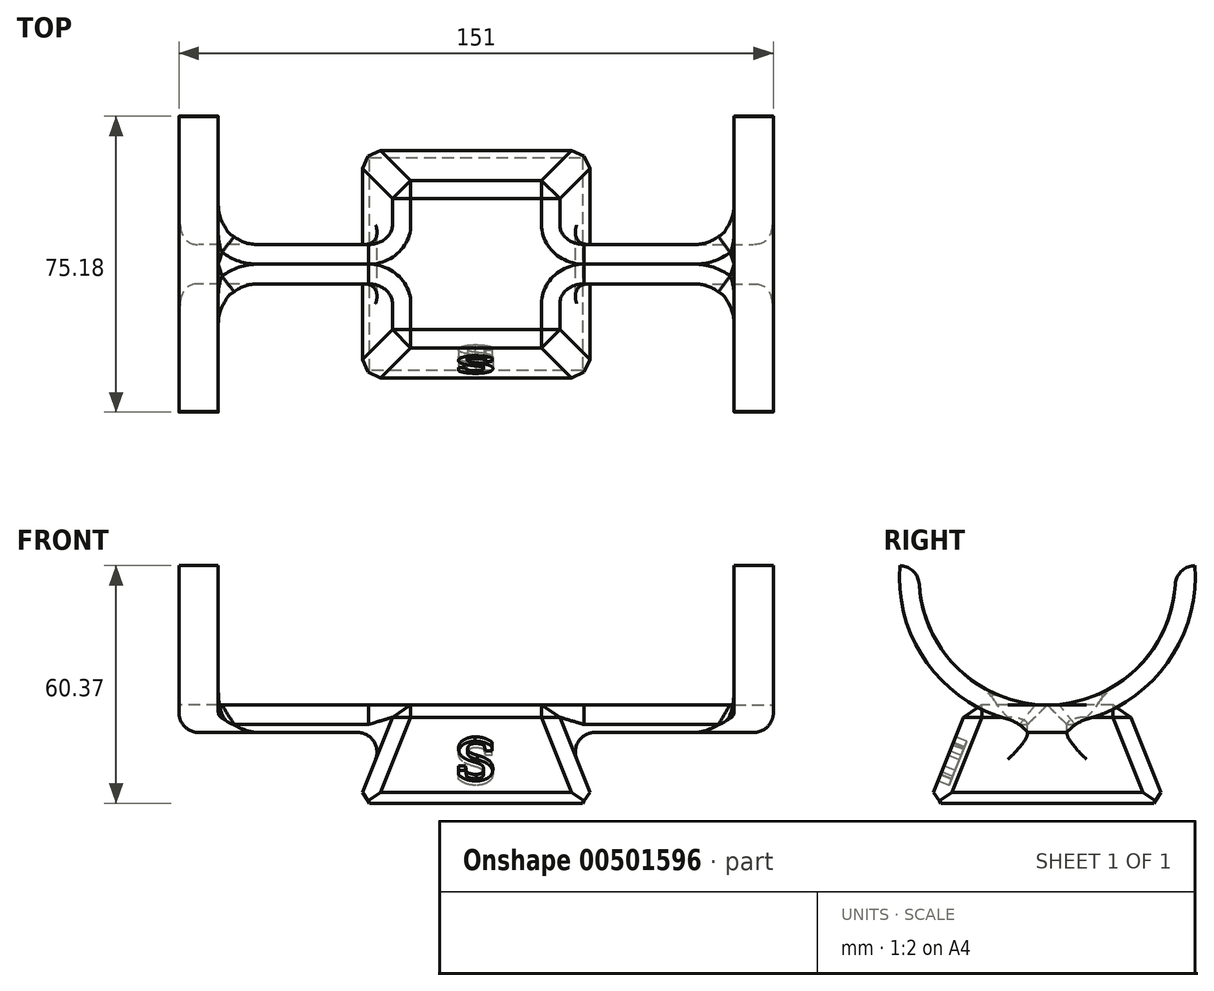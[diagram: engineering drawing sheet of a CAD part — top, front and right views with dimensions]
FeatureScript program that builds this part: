
annotation { "Feature Type Name" : "Feature", "Feature Type Description" : "" }
export const myFeature = defineFeature(function(context is Context, id is Id, definition is map)
    precondition{}
    {
        {
            var Q0;
            Q0=qCreatedBy(makeId("Top.planeOp"),FACE);
            var sketch = newSketch(context, id + "F0", { "sketchPlane" : qUnion([Q0])});
            skLineSegment(sketch, "E0.bottom", {"start": v(-30, 30) * mm, "end": v(30, 30) * mm});
            skLineSegment(sketch, "E0.top", {"start": v(-30, -30) * mm, "end": v(30, -30) * mm});
            skLineSegment(sketch, "E0.left", {"start": v(-30, 30) * mm, "end": v(-30, -30) * mm});
            skLineSegment(sketch, "E0.right", {"start": v(30, 30) * mm, "end": v(30, -30) * mm});
            skPoint(sketch, "E0.middle", {"position": v(0, 0) * mm});
            skSolve(sketch);
        }
        {
            var Q0;
            Q0=qCreatedBy(makeId("Top.planeOp"),FACE);
            cPlane(context, id + "F1", {"entities" : qUnion([Q0]), "cplaneType" : CPlaneType.OFFSET, "offset" : 25 * mm, "width" : 150 * mm, "height" : 150 * mm});
        }
        {
            var Q0;
            Q0=qCreatedBy(id+"F1.planeOp",FACE);
            var sketch = newSketch(context, id + "F2", { "sketchPlane" : qUnion([Q0])});
            skLineSegment(sketch, "E1.bottom", {"start": v(-20, 20) * mm, "end": v(20, 20) * mm});
            skLineSegment(sketch, "E1.top", {"start": v(-20, -20) * mm, "end": v(20, -20) * mm});
            skLineSegment(sketch, "E1.left", {"start": v(-20, 20) * mm, "end": v(-20, -20) * mm});
            skLineSegment(sketch, "E1.right", {"start": v(20, 20) * mm, "end": v(20, -20) * mm});
            skPoint(sketch, "E1.middle", {"position": v(0, 0) * mm});
            skSolve(sketch);
        }
        {
            var Q0;
            Q0=makeQuery(id+"F0.imprint","IMPRINT",FACE,{"disambiguationData":[TD([[makeQuery(id+"F0.imprint","IMPRINT",EDGE,{"derivedFrom":sQuery(id+"F0.wireOp",EDGE,"E0.bottom")}),-1.0]])]});
            var Q1;
            Q1=makeQuery(id+"F2.imprint","IMPRINT",FACE,{"disambiguationData":[TD([[makeQuery(id+"F2.imprint","IMPRINT",EDGE,{"derivedFrom":sQuery(id+"F2.wireOp",EDGE,"E1.bottom")}),-1.0]])]});
            loft(context, id + "F3", {"sheetProfilesArray" : [{ "sheetProfileEntities" : qUnion([Q0]) }, { "sheetProfileEntities" : qUnion([Q1]) }]});
        }
        {
            var Q0;
            Q0=qCreatedBy(id+"F1.planeOp",FACE);
            var sketch = newSketch(context, id + "F4", { "sketchPlane" : qUnion([Q0])});
            skLineSegment(sketch, "E2.bottom", {"start": v(-75.5, 5) * mm, "end": v(75.5, 5) * mm});
            skLineSegment(sketch, "E2.top", {"start": v(-75.5, -5) * mm, "end": v(75.5, -5) * mm});
            skLineSegment(sketch, "E2.left", {"start": v(-75.5, 5) * mm, "end": v(-75.5, -5) * mm});
            skLineSegment(sketch, "E2.right", {"start": v(75.5, 5) * mm, "end": v(75.5, -5) * mm});
            skPoint(sketch, "E2.middle", {"position": v(0, 0) * mm});
            skSolve(sketch);
        }
        {
            var Q0;
            Q0=makeQuery(id+"F4.imprint","IMPRINT",FACE,{"disambiguationData":[TD([[makeQuery(id+"F4.imprint","IMPRINT",EDGE,{"derivedFrom":sQuery(id+"F4.wireOp",EDGE,"E2.bottom")}),-1.0]])]});
            extrude(context, id + "F5", {"entities" : qUnion([Q0]), "operationType" : NewBodyOperationType.ADD, "oppositeDirection" : true, "depth" : 7 * mm});
        }
        {
            var Q0;
            Q0=makeQuery(id+"F5.opExtrude","SWEPT_FACE",FACE,{"disambiguationData":[OSD([sQuery(id+"F4.wireOp",EDGE,"E2.right")])]});
            var sketch = newSketch(context, id + "F6", { "sketchPlane" : qUnion([Q0])});
            skArc(sketch, "E3", {"start": v(-32.5, 60) * mm, "mid": v(-23.88, 35.41) * mm, "end": v(0, 25) * mm});
            skArc(sketch, "E4.MirrorCS", {"start": v(32.5, 60) * mm, "mid": v(23.88, 35.41) * mm, "end": v(0, 25) * mm});
            skArc(sketch, "E5.0", {"start": v(37.49, 60.37) * mm, "mid": v(27.55, 32.01) * mm, "end": v(0, 20) * mm});
            skArc(sketch, "E5.1", {"start": v(-37.49, 60.37) * mm, "mid": v(-27.55, 32.01) * mm, "end": v(0, 20) * mm});
            skLineSegment(sketch, "E6", {"start": v(-32.5, 60) * mm, "end": v(-37.49, 60.37) * mm});
            skLineSegment(sketch, "E7", {"start": v(32.5, 60) * mm, "end": v(37.49, 60.37) * mm});
            skSolve(sketch);
        }
        {
            var Q0;
            Q0 = qSketchRegion(id + "F6", true);
            extrude(context, id + "F7", {"entities" : qUnion([Q0]), "operationType" : NewBodyOperationType.ADD, "oppositeDirection" : true, "depth" : 10 * mm});
        }
        {
            var Q0;
            {var subQ0=sQuery(id+"F4.wireOp",EDGE,"E2.right");var subQ2=sQuery(id+"F4.wireOp",EDGE,"E2.top");Q0=makeQuery(id+"F7.boolean.opBoolean","INTERSECT",EDGE,{"derivedFrom":[makeQuery(id+"F5.boolean.opBoolean","SPLIT",FACE,{"disambiguationData":[TD([makeQuery(id+"F5.opExtrude","SWEPT_FACE",FACE,{"disambiguationData":[OSD([subQ0])]})])],"derivedFrom":makeQuery(id+"F5.opExtrude","SWEPT_FACE",FACE,{"disambiguationData":[OSD([subQ2])]})}),makeQuery(id+"F7.opExtrude","SWEPT_FACE",FACE,{"disambiguationData":[OSD([sQuery(id+"F6.wireOp",EDGE,"E5.0"),sQuery(id+"F6.wireOp",EDGE,"E5.1")])]})]});}
            var Q1;
            {var subQ0=sQuery(id+"F4.wireOp",EDGE,"E2.right");var subQ3=sQuery(id+"F4.wireOp",EDGE,"E2.bottom");Q1=makeQuery(id+"F7.boolean.opBoolean","INTERSECT",EDGE,{"derivedFrom":[makeQuery(id+"F5.boolean.opBoolean","SPLIT",FACE,{"disambiguationData":[TD([makeQuery(id+"F5.opExtrude","SWEPT_FACE",FACE,{"disambiguationData":[OSD([subQ0])]})])],"derivedFrom":makeQuery(id+"F5.opExtrude","SWEPT_FACE",FACE,{"disambiguationData":[OSD([subQ3])]})}),makeQuery(id+"F7.opExtrude","SWEPT_FACE",FACE,{"disambiguationData":[OSD([sQuery(id+"F6.wireOp",EDGE,"E5.0"),sQuery(id+"F6.wireOp",EDGE,"E5.1")])]})]});}
            var Q2;
            {var subQ0=sQuery(id+"F4.wireOp",EDGE,"E2.right");var subQ3=sQuery(id+"F4.wireOp",EDGE,"E2.bottom");Q2=makeQuery(id+"F7.boolean.opBoolean","INTERSECT",EDGE,{"derivedFrom":[makeQuery(id+"F5.boolean.opBoolean","SPLIT",FACE,{"disambiguationData":[TD([makeQuery(id+"F5.opExtrude","SWEPT_FACE",FACE,{"disambiguationData":[OSD([subQ0])]})])],"derivedFrom":makeQuery(id+"F5.opExtrude","SWEPT_FACE",FACE,{"disambiguationData":[OSD([subQ3])]})}),makeQuery(id+"F7.opExtrude","CAP_FACE",FACE,{"disambiguationData":[OSD([sQuery(id+"F6.wireOp",EDGE,"E3"),sQuery(id+"F6.wireOp",EDGE,"E4.MirrorCS"),sQuery(id+"F6.wireOp",EDGE,"E5.0"),sQuery(id+"F6.wireOp",EDGE,"E5.1"),sQuery(id+"F6.wireOp",EDGE,"E6"),sQuery(id+"F6.wireOp",EDGE,"E7")])],"isStart":false})]});}
            var Q3;
            {var subQ0=sQuery(id+"F4.wireOp",EDGE,"E2.right");var subQ2=sQuery(id+"F4.wireOp",EDGE,"E2.top");Q3=makeQuery(id+"F7.boolean.opBoolean","INTERSECT",EDGE,{"derivedFrom":[makeQuery(id+"F5.boolean.opBoolean","SPLIT",FACE,{"disambiguationData":[TD([makeQuery(id+"F5.opExtrude","SWEPT_FACE",FACE,{"disambiguationData":[OSD([subQ0])]})])],"derivedFrom":makeQuery(id+"F5.opExtrude","SWEPT_FACE",FACE,{"disambiguationData":[OSD([subQ2])]})}),makeQuery(id+"F7.opExtrude","CAP_FACE",FACE,{"disambiguationData":[OSD([sQuery(id+"F6.wireOp",EDGE,"E3"),sQuery(id+"F6.wireOp",EDGE,"E4.MirrorCS"),sQuery(id+"F6.wireOp",EDGE,"E5.0"),sQuery(id+"F6.wireOp",EDGE,"E5.1"),sQuery(id+"F6.wireOp",EDGE,"E6"),sQuery(id+"F6.wireOp",EDGE,"E7")])],"isStart":false})]});}
            fillet(context, id + "F8", {"entities" : qUnion([Q0, Q1, Q2, Q3]), "radius" : 10 * mm, "tangentPropagation" : true, "allowEdgeOverflow" : false});
        }
        {
            var Q0;
            Q0=makeQuery(id+"F7.boolean.opBoolean","INTERSECT",EDGE,{"disambiguationData":[OD(1.0)],"derivedFrom":[makeQuery(id+"F5.boolean.opBoolean","MERGE",FACE,{"derivedFrom":[makeQuery(id+"F3.opLoft","CAP_FACE",FACE,{"disambiguationData":[OSD([makeQuery(id+"F2.imprint","IMPRINT",FACE,{"disambiguationData":[TD([[makeQuery(id+"F2.imprint","IMPRINT",EDGE,{"derivedFrom":sQuery(id+"F2.wireOp",EDGE,"E1.bottom")}),-1.0]])]})])],"isStart":true}),makeQuery(id+"F5.opExtrude","CAP_FACE",FACE,{"disambiguationData":[OSD([sQuery(id+"F4.wireOp",EDGE,"E2.bottom"),sQuery(id+"F4.wireOp",EDGE,"E2.top"),sQuery(id+"F4.wireOp",EDGE,"E2.left"),sQuery(id+"F4.wireOp",EDGE,"E2.right")])],"isStart":true})]}),makeQuery(id+"F7.opExtrude","CAP_FACE",FACE,{"disambiguationData":[OSD([sQuery(id+"F6.wireOp",EDGE,"E3"),sQuery(id+"F6.wireOp",EDGE,"E4.MirrorCS"),sQuery(id+"F6.wireOp",EDGE,"E5.0"),sQuery(id+"F6.wireOp",EDGE,"E5.1"),sQuery(id+"F6.wireOp",EDGE,"E6"),sQuery(id+"F6.wireOp",EDGE,"E7")])],"isStart":false})]});
            fillet(context, id + "F9", {"entities" : qUnion([Q0]), "radius" : 3 * mm, "tangentPropagation" : true, "allowEdgeOverflow" : false});
        }
        {
            var Q0;
            Q0=makeQuery(id+"F5.opExtrude","CAP_EDGE",EDGE,{"disambiguationData":[OSD([sQuery(id+"F4.wireOp",EDGE,"E2.right")])],"isStart":false});
            var Q1;
            Q1=makeQuery(id+"F5.boolean.opBoolean","INTERSECT",EDGE,{"derivedFrom":[makeQuery(id+"F3.opLoft","SWEPT_FACE",FACE,{"disambiguationData":[OSD([sQuery(id+"F0.wireOp",EDGE,"E0.bottom"),sQuery(id+"F0.wireOp",EDGE,"E0.top"),sQuery(id+"F0.wireOp",EDGE,"E0.right"),sQuery(id+"F2.wireOp",EDGE,"E1.bottom"),sQuery(id+"F2.wireOp",EDGE,"E1.top"),sQuery(id+"F2.wireOp",EDGE,"E1.right")])]}),makeQuery(id+"F5.opExtrude","SWEPT_FACE",FACE,{"disambiguationData":[OSD([sQuery(id+"F4.wireOp",EDGE,"E2.bottom")])]})]});
            var Q2;
            Q2=makeQuery(id+"F5.boolean.opBoolean","INTERSECT",EDGE,{"derivedFrom":[makeQuery(id+"F3.opLoft","SWEPT_FACE",FACE,{"disambiguationData":[OSD([sQuery(id+"F0.wireOp",EDGE,"E0.bottom"),sQuery(id+"F0.wireOp",EDGE,"E0.top"),sQuery(id+"F0.wireOp",EDGE,"E0.right"),sQuery(id+"F2.wireOp",EDGE,"E1.bottom"),sQuery(id+"F2.wireOp",EDGE,"E1.top"),sQuery(id+"F2.wireOp",EDGE,"E1.right")])]}),makeQuery(id+"F5.opExtrude","CAP_FACE",FACE,{"disambiguationData":[OSD([sQuery(id+"F4.wireOp",EDGE,"E2.bottom"),sQuery(id+"F4.wireOp",EDGE,"E2.top"),sQuery(id+"F4.wireOp",EDGE,"E2.left"),sQuery(id+"F4.wireOp",EDGE,"E2.right")])],"isStart":false})]});
            var Q3;
            Q3=makeQuery(id+"F5.boolean.opBoolean","INTERSECT",EDGE,{"derivedFrom":[makeQuery(id+"F3.opLoft","SWEPT_FACE",FACE,{"disambiguationData":[OSD([sQuery(id+"F0.wireOp",EDGE,"E0.bottom"),sQuery(id+"F0.wireOp",EDGE,"E0.top"),sQuery(id+"F0.wireOp",EDGE,"E0.right"),sQuery(id+"F2.wireOp",EDGE,"E1.bottom"),sQuery(id+"F2.wireOp",EDGE,"E1.top"),sQuery(id+"F2.wireOp",EDGE,"E1.right")])]}),makeQuery(id+"F5.opExtrude","SWEPT_FACE",FACE,{"disambiguationData":[OSD([sQuery(id+"F4.wireOp",EDGE,"E2.top")])]})]});
            var Q4;
            Q4=makeQuery(id+"F7.opExtrude","SWEPT_EDGE",EDGE,{"disambiguationData":[OSD([sQuery(id+"F6.wireOp",EDGE,"E4.MirrorCS"),sQuery(id+"F6.wireOp",EDGE,"E7")])]});
            var Q5;
            Q5=makeQuery(id+"F7.opExtrude","SWEPT_EDGE",EDGE,{"disambiguationData":[OSD([sQuery(id+"F6.wireOp",EDGE,"E3"),sQuery(id+"F6.wireOp",EDGE,"E6")])]});
            fillet(context, id + "F10", {"entities" : qUnion([Q0, Q1, Q2, Q3, Q4, Q5]), "radius" : 5 * mm, "tangentPropagation" : true, "allowEdgeOverflow" : false});
        }
        {
            var Q0;
            Q0=makeQuery(id+"F3.opLoft","SWEPT_BODY",BODY,{"disambiguationData":[OSD([makeQuery(id+"F0.imprint","IMPRINT",FACE,{"disambiguationData":[TD([[makeQuery(id+"F0.imprint","IMPRINT",EDGE,{"derivedFrom":sQuery(id+"F0.wireOp",EDGE,"E0.bottom")}),-1.0]])]}),makeQuery(id+"F2.imprint","IMPRINT",FACE,{"disambiguationData":[TD([[makeQuery(id+"F2.imprint","IMPRINT",EDGE,{"derivedFrom":sQuery(id+"F2.wireOp",EDGE,"E1.bottom")}),-1.0]])]})])]});
            var Q1;
            Q1=qCreatedBy(makeId("Right.planeOp"),FACE);
            mirror(context, id + "F11", {"operationType" : NewBodyOperationType.ADD, "entities" : qUnion([Q0]), "mirrorPlane" : qUnion([Q1])});
        }
        {
            var Q0;
            Q0=makeQuery(id+"F3.opLoft","MID_CAP_EDGE",EDGE,{"disambiguationData":[OSD([sQuery(id+"F2.wireOp",EDGE,"E1.top"),sQuery(id+"F2.wireOp",EDGE,"E1.left"),sQuery(id+"F2.wireOp",EDGE,"E1.right")])],"capPos":1.0});
            var Q1;
            Q1=makeQuery(id+"F3.opLoft","MID_CAP_EDGE",EDGE,{"disambiguationData":[OSD([sQuery(id+"F2.wireOp",EDGE,"E1.bottom"),sQuery(id+"F2.wireOp",EDGE,"E1.left"),sQuery(id+"F2.wireOp",EDGE,"E1.right")])],"capPos":1.0});
            var Q2;
            Q2=makeQuery(id+"F3.opLoft","SWEPT_EDGE",EDGE,{"disambiguationData":[OSD([sQuery(id+"F0.wireOp",EDGE,"E0.bottom"),sQuery(id+"F0.wireOp",EDGE,"E0.right"),sQuery(id+"F2.wireOp",EDGE,"E1.bottom"),sQuery(id+"F2.wireOp",EDGE,"E1.right")])]});
            var Q3;
            Q3=makeQuery(id+"F3.opLoft","SWEPT_EDGE",EDGE,{"disambiguationData":[OSD([sQuery(id+"F0.wireOp",EDGE,"E0.bottom"),sQuery(id+"F0.wireOp",EDGE,"E0.left"),sQuery(id+"F2.wireOp",EDGE,"E1.bottom"),sQuery(id+"F2.wireOp",EDGE,"E1.left")])]});
            var Q4;
            Q4=makeQuery(id+"F3.opLoft","SWEPT_EDGE",EDGE,{"disambiguationData":[OSD([sQuery(id+"F0.wireOp",EDGE,"E0.top"),sQuery(id+"F0.wireOp",EDGE,"E0.left"),sQuery(id+"F2.wireOp",EDGE,"E1.top"),sQuery(id+"F2.wireOp",EDGE,"E1.left")])]});
            var Q5;
            Q5=makeQuery(id+"F3.opLoft","SWEPT_EDGE",EDGE,{"disambiguationData":[OSD([sQuery(id+"F0.wireOp",EDGE,"E0.top"),sQuery(id+"F0.wireOp",EDGE,"E0.right"),sQuery(id+"F2.wireOp",EDGE,"E1.top"),sQuery(id+"F2.wireOp",EDGE,"E1.right")])]});
            var Q6;
            {var subQ0=sQuery(id+"F4.wireOp",EDGE,"E2.left");var subQ1=sQuery(id+"F4.wireOp",EDGE,"E2.bottom");Q6=makeQuery(id+"F5.boolean.opBoolean","SPLIT",EDGE,{"disambiguationData":[TD([makeQuery(id+"F5.opExtrude","SWEPT_FACE",FACE,{"disambiguationData":[OSD([subQ0])]})])],"derivedFrom":makeQuery(id+"F5.opExtrude","CAP_EDGE",EDGE,{"disambiguationData":[OSD([subQ1])],"isStart":true})});}
            var Q7;
            {var subQ0=sQuery(id+"F4.wireOp",EDGE,"E2.left");var subQ1=sQuery(id+"F4.wireOp",EDGE,"E2.top");Q7=makeQuery(id+"F5.boolean.opBoolean","SPLIT",EDGE,{"disambiguationData":[TD([makeQuery(id+"F5.opExtrude","SWEPT_FACE",FACE,{"disambiguationData":[OSD([subQ0])]})])],"derivedFrom":makeQuery(id+"F5.opExtrude","CAP_EDGE",EDGE,{"disambiguationData":[OSD([subQ1])],"isStart":true})});}
            var Q8;
            {var subQ0=sQuery(id+"F4.wireOp",EDGE,"E2.right");var subQ1=sQuery(id+"F4.wireOp",EDGE,"E2.bottom");Q8=makeQuery(id+"F5.boolean.opBoolean","SPLIT",EDGE,{"disambiguationData":[TD([makeQuery(id+"F5.opExtrude","SWEPT_FACE",FACE,{"disambiguationData":[OSD([subQ0])]})])],"derivedFrom":makeQuery(id+"F5.opExtrude","CAP_EDGE",EDGE,{"disambiguationData":[OSD([subQ1])],"isStart":true})});}
            var Q9;
            {var subQ0=sQuery(id+"F4.wireOp",EDGE,"E2.top");var subQ1=sQuery(id+"F4.wireOp",EDGE,"E2.right");Q9=makeQuery(id+"F5.boolean.opBoolean","SPLIT",EDGE,{"disambiguationData":[TD([makeQuery(id+"F5.opExtrude","SWEPT_FACE",FACE,{"disambiguationData":[OSD([subQ1])]})])],"derivedFrom":makeQuery(id+"F5.opExtrude","CAP_EDGE",EDGE,{"disambiguationData":[OSD([subQ0])],"isStart":true})});}
            chamfer(context, id + "F12", {"entities" : qUnion([Q0, Q1, Q2, Q3, Q4, Q5, Q6, Q7, Q8, Q9]), "width" : 5 * mm, "tangentPropagation" : true});
        }
        {
            var Q0;
            Q0=makeQuery(id+"F11.opPattern","COPY",EDGE,{"derivedFrom":makeQuery(id+"F5.opExtrude","CAP_EDGE",EDGE,{"disambiguationData":[OSD([sQuery(id+"F4.wireOp",EDGE,"E2.left")])],"isStart":false}),"instanceName":"1"});
            var Q1;
            Q1=makeQuery(id+"F5.opExtrude","CAP_EDGE",EDGE,{"disambiguationData":[OSD([sQuery(id+"F4.wireOp",EDGE,"E2.left")])],"isStart":false});
            fillet(context, id + "F13", {"entities" : qUnion([Q0, Q1]), "radius" : 5 * mm, "tangentPropagation" : true, "allowEdgeOverflow" : false});
        }
        {
            var Q0;
            Q0=makeQuery(id+"F3.opLoft","MID_CAP_EDGE",EDGE,{"disambiguationData":[OSD([sQuery(id+"F0.wireOp",EDGE,"E0.bottom"),sQuery(id+"F0.wireOp",EDGE,"E0.left"),sQuery(id+"F0.wireOp",EDGE,"E0.right")])],"capPos":0.0});
            var Q1;
            Q1=makeQuery(id+"F3.opLoft","MID_CAP_EDGE",EDGE,{"disambiguationData":[OSD([sQuery(id+"F0.wireOp",EDGE,"E0.bottom"),sQuery(id+"F0.wireOp",EDGE,"E0.top"),sQuery(id+"F0.wireOp",EDGE,"E0.right")])],"capPos":0.0});
            var Q2;
            Q2=makeQuery(id+"F3.opLoft","MID_CAP_EDGE",EDGE,{"disambiguationData":[OSD([sQuery(id+"F0.wireOp",EDGE,"E0.top"),sQuery(id+"F0.wireOp",EDGE,"E0.left"),sQuery(id+"F0.wireOp",EDGE,"E0.right")])],"capPos":0.0});
            var Q3;
            Q3=makeQuery(id+"F3.opLoft","MID_CAP_EDGE",EDGE,{"disambiguationData":[OSD([sQuery(id+"F0.wireOp",EDGE,"E0.bottom"),sQuery(id+"F0.wireOp",EDGE,"E0.top"),sQuery(id+"F0.wireOp",EDGE,"E0.left")])],"capPos":0.0});
            chamfer(context, id + "F14", {"entities" : qUnion([Q0, Q1, Q2, Q3]), "width" : 2 * mm, "tangentPropagation" : true});
        }
        {
            var Q0;
            Q0=makeQuery(id+"F3.opLoft","SWEPT_FACE",FACE,{"disambiguationData":[OSD([sQuery(id+"F0.wireOp",EDGE,"E0.top"),sQuery(id+"F0.wireOp",EDGE,"E0.left"),sQuery(id+"F0.wireOp",EDGE,"E0.right"),sQuery(id+"F2.wireOp",EDGE,"E1.top"),sQuery(id+"F2.wireOp",EDGE,"E1.left"),sQuery(id+"F2.wireOp",EDGE,"E1.right")])]});
            var sketch = newSketch(context, id + "F15", { "sketchPlane" : qUnion([Q0])});
            skLineSegment(sketch, "E8", {"start": v(0, -11.28) * mm, "end": v(0, 10.78) * mm});
            skText(sketch, "E9", { "text": "S", "fontName": "RobotoSlab-Bold.ttf"});
            const initialGuessF15  = {"E9": [-0.00527, -0.00485, 1, 0, 0.01187]};
            skSetInitialGuess(sketch, initialGuessF15);
            skSolve(sketch);
        }
        {
            var Q0;
            {var subQ6=sQuery(id+"F15.wireOp",EDGE,"E9.sketch_text.stroke-4");Q0=makeQuery(id+"F15.imprint","IMPRINT",FACE,{"disambiguationData":[TD([[makeQuery(id+"F15.imprint","IMPRINT",EDGE,{"derivedFrom":subQ6}),-1.0]])]});}
            var Q1;
            Q1=makeQuery(id+"F15.imprint","IMPRINT",FACE,{"disambiguationData":[TD([[makeQuery(id+"F15.imprint","IMPRINT",EDGE,{"derivedFrom":sQuery(id+"F15.wireOp",EDGE,"E9.sketch_text.stroke-0")}),-1.0]])]});
            var Q2;
            {var subQ8=sQuery(id+"F15.wireOp",EDGE,"E9.sketch_text.stroke-8");Q2=makeQuery(id+"F15.imprint","IMPRINT",FACE,{"disambiguationData":[TD([[makeQuery(id+"F15.imprint","IMPRINT",EDGE,{"derivedFrom":subQ8}),-1.0]])]});}
            var Q3;
            {var subQ5=sQuery(id+"F15.wireOp",EDGE,"E9.sketch_text.stroke-12");Q3=makeQuery(id+"F15.imprint","IMPRINT",FACE,{"disambiguationData":[TD([[makeQuery(id+"F15.imprint","IMPRINT",EDGE,{"derivedFrom":subQ5}),-1.0]])]});}
            extrude(context, id + "F16", {"entities" : qUnion([Q0, Q1, Q2, Q3]), "operationType" : NewBodyOperationType.REMOVE, "oppositeDirection" : true, "depth" : 3 * mm});
        }
    });
